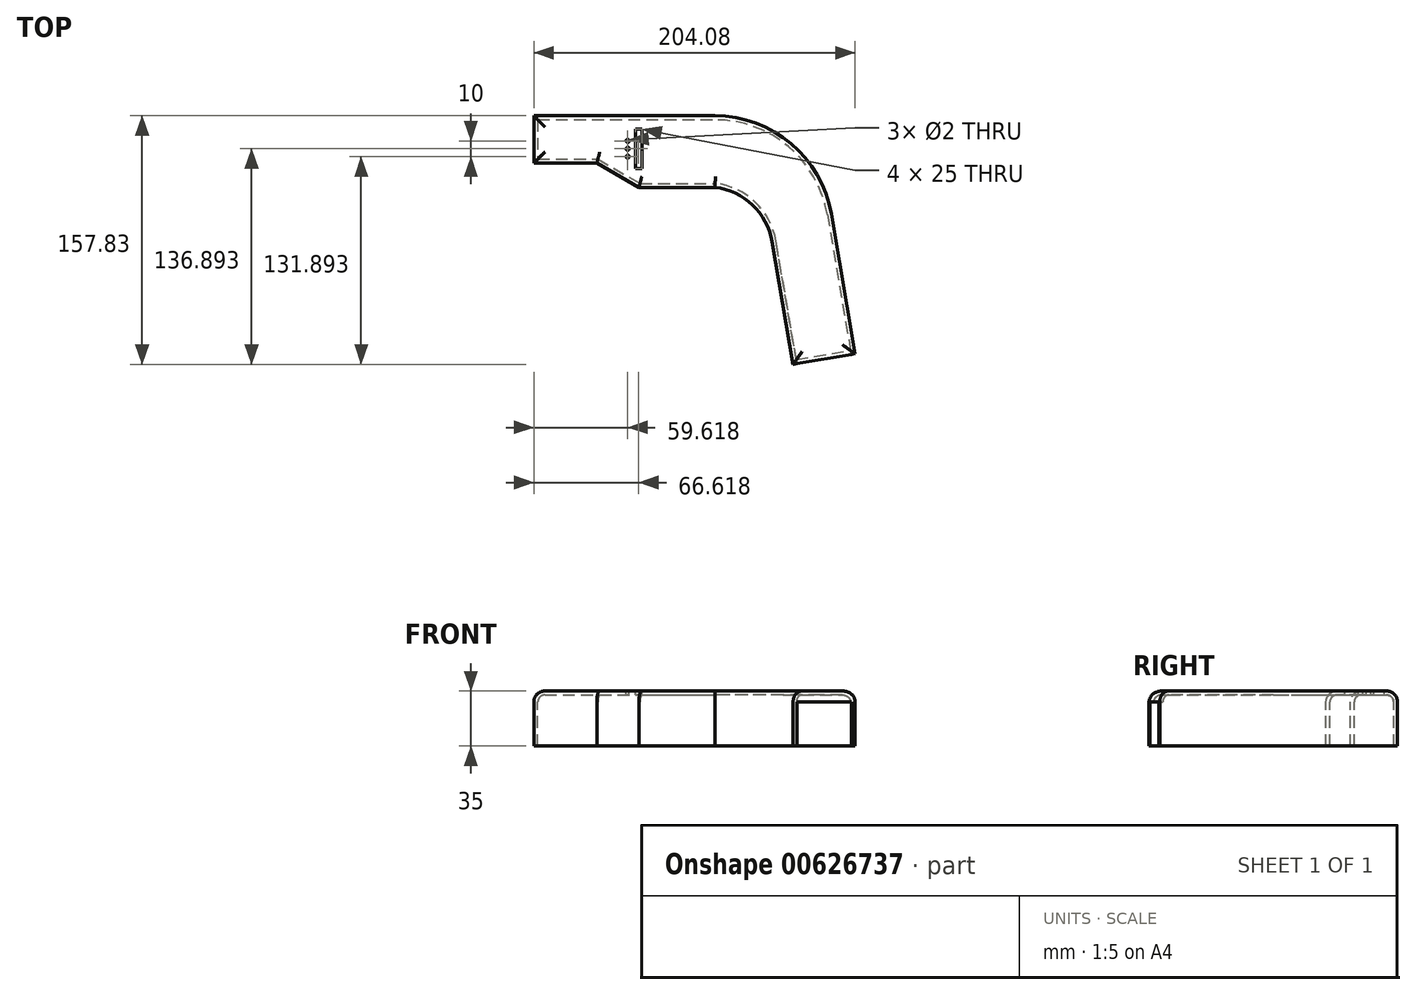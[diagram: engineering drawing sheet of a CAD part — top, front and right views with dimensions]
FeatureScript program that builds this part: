
annotation { "Feature Type Name" : "Feature", "Feature Type Description" : "" }
export const myFeature = defineFeature(function(context is Context, id is Id, definition is map)
    precondition{}
    {
        {
            var Q0;
            Q0=qCreatedBy(makeId("Top.planeOp"),FACE);
            var sketch = newSketch(context, id + "F0", { "sketchPlane" : qUnion([Q0])});
            skLineSegment(sketch, "E0", {"start": v(-99.8, 51.85) * mm, "end": v(15.2, 51.85) * mm});
            skLineSegment(sketch, "E1", {"start": v(-99.8, 51.85) * mm, "end": v(-99.8, 21.85) * mm});
            skLineSegment(sketch, "E2", {"start": v(-99.8, 21.85) * mm, "end": v(-59.8, 21.85) * mm});
            skArc(sketch, "E3", {"start": v(89.14, -10.53) * mm, "mid": v(63.57, 34.17) * mm, "end": v(15.2, 51.85) * mm});
            skLineSegment(sketch, "E4", {"start": v(89.14, -10.53) * mm, "end": v(104.28, -99.25) * mm});
            skLineSegment(sketch, "E5", {"start": v(104.28, -99.25) * mm, "end": v(64.85, -105.98) * mm});
            skLineSegment(sketch, "E6", {"start": v(-59.8, 21.85) * mm, "end": v(-33.06, 6.41) * mm});
            skLineSegment(sketch, "E7", {"start": v(-33.06, 6.41) * mm, "end": v(15.2, 6.41) * mm});
            skLineSegment(sketch, "E8", {"start": v(64.85, -105.98) * mm, "end": v(51.56, -28.12) * mm});
            skArc(sketch, "E9", {"start": v(51.56, -28.12) * mm, "mid": v(39.12, -4.81) * mm, "end": v(15.2, 6.41) * mm});
            skSolve(sketch);
        }
        {
            var Q0;
            Q0=makeQuery(id+"F0.imprint","IMPRINT",FACE,{"disambiguationData":[TD([[makeQuery(id+"F0.imprint","IMPRINT",EDGE,{"derivedFrom":sQuery(id+"F0.wireOp",EDGE,"E0")}),-1.0]])]});
            extrude(context, id + "F1", {"entities" : qUnion([Q0]), "oppositeDirection" : true, "depth" : 35 * mm, "offsetDistance" : 25 * mm});
        }
        {
            var Q0;
            Q0=makeQuery(id+"F1.opExtrude","CAP_FACE",FACE,{"disambiguationData":[OSD([sQuery(id+"F0.wireOp",EDGE,"E0"),sQuery(id+"F0.wireOp",EDGE,"E1"),sQuery(id+"F0.wireOp",EDGE,"E2"),sQuery(id+"F0.wireOp",EDGE,"E3"),sQuery(id+"F0.wireOp",EDGE,"E4"),sQuery(id+"F0.wireOp",EDGE,"E5"),sQuery(id+"F0.wireOp",EDGE,"E6"),sQuery(id+"F0.wireOp",EDGE,"E7"),sQuery(id+"F0.wireOp",EDGE,"E8"),sQuery(id+"F0.wireOp",EDGE,"E9")])],"isStart":true});
            fillet(context, id + "F2", {"entities" : qUnion([Q0]), "radius" : 7 * mm, "tangentPropagation" : true, "allowEdgeOverflow" : false});
        }
        {
            var Q0;
            Q0=makeQuery(id+"F1.opExtrude","CAP_FACE",FACE,{"disambiguationData":[OSD([sQuery(id+"F0.wireOp",EDGE,"E0"),sQuery(id+"F0.wireOp",EDGE,"E1"),sQuery(id+"F0.wireOp",EDGE,"E2"),sQuery(id+"F0.wireOp",EDGE,"E3"),sQuery(id+"F0.wireOp",EDGE,"E4"),sQuery(id+"F0.wireOp",EDGE,"E5"),sQuery(id+"F0.wireOp",EDGE,"E6"),sQuery(id+"F0.wireOp",EDGE,"E7"),sQuery(id+"F0.wireOp",EDGE,"E8"),sQuery(id+"F0.wireOp",EDGE,"E9")])],"isStart":false});
            var Q1;
            Q1=makeQuery(id+"F1.opExtrude","SWEPT_FACE",FACE,{"disambiguationData":[OSD([sQuery(id+"F0.wireOp",EDGE,"E5")])]});
            shell(context, id + "F3", {"entities" : qUnion([Q0, Q1]), "thickness" : 2.5 * mm});
        }
        {
            var Q0;
            Q0=makeQuery(id+"F1.opExtrude","CAP_FACE",FACE,{"disambiguationData":[OSD([sQuery(id+"F0.wireOp",EDGE,"E0"),sQuery(id+"F0.wireOp",EDGE,"E1"),sQuery(id+"F0.wireOp",EDGE,"E2"),sQuery(id+"F0.wireOp",EDGE,"E3"),sQuery(id+"F0.wireOp",EDGE,"E4"),sQuery(id+"F0.wireOp",EDGE,"E5"),sQuery(id+"F0.wireOp",EDGE,"E6"),sQuery(id+"F0.wireOp",EDGE,"E7"),sQuery(id+"F0.wireOp",EDGE,"E8"),sQuery(id+"F0.wireOp",EDGE,"E9")])],"isStart":true});
            var sketch = newSketch(context, id + "F4", { "sketchPlane" : qUnion([Q0])});
            skLineSegment(sketch, "E10.bottom", {"start": v(-31.18, 18.41) * mm, "end": v(-35.18, 18.41) * mm});
            skLineSegment(sketch, "E10.top", {"start": v(-31.18, 43.41) * mm, "end": v(-35.18, 43.41) * mm});
            skLineSegment(sketch, "E10.left", {"start": v(-31.18, 18.41) * mm, "end": v(-31.18, 43.41) * mm});
            skLineSegment(sketch, "E10.right", {"start": v(-35.18, 18.41) * mm, "end": v(-35.18, 43.41) * mm});
            skCircle(sketch, "E11", {"center": v(-40.18, 35.91) * mm, "radius": 1 * mm});
            skCircle(sketch, "E12", {"center": v(-40.18, 30.91) * mm, "radius": 1 * mm});
            skCircle(sketch, "E13", {"center": v(-40.18, 25.91) * mm, "radius": 1 * mm});
            skSolve(sketch);
        }
        {
            var Q0;
            Q0=makeQuery(id+"F4.imprint","IMPRINT",FACE,{"disambiguationData":[TD([[makeQuery(id+"F4.imprint","IMPRINT",EDGE,{"derivedFrom":sQuery(id+"F4.wireOp",EDGE,"E11")}),1.0]])]});
            var Q1;
            Q1=makeQuery(id+"F4.imprint","IMPRINT",FACE,{"disambiguationData":[TD([[makeQuery(id+"F4.imprint","IMPRINT",EDGE,{"derivedFrom":sQuery(id+"F4.wireOp",EDGE,"E12")}),1.0]])]});
            var Q2;
            Q2=makeQuery(id+"F4.imprint","IMPRINT",FACE,{"disambiguationData":[TD([[makeQuery(id+"F4.imprint","IMPRINT",EDGE,{"derivedFrom":sQuery(id+"F4.wireOp",EDGE,"E13")}),1.0]])]});
            var Q3;
            Q3=makeQuery(id+"F4.imprint","IMPRINT",FACE,{"disambiguationData":[TD([[makeQuery(id+"F4.imprint","IMPRINT",EDGE,{"derivedFrom":sQuery(id+"F4.wireOp",EDGE,"E10.bottom")}),-1.0]])]});
            extrude(context, id + "F5", {"entities" : qUnion([Q0, Q1, Q2, Q3]), "operationType" : NewBodyOperationType.REMOVE, "endBound" : BoundingType.THROUGH_ALL, "oppositeDirection" : true, "depth" : 25 * mm, "offsetDistance" : 25 * mm});
        }
    });
